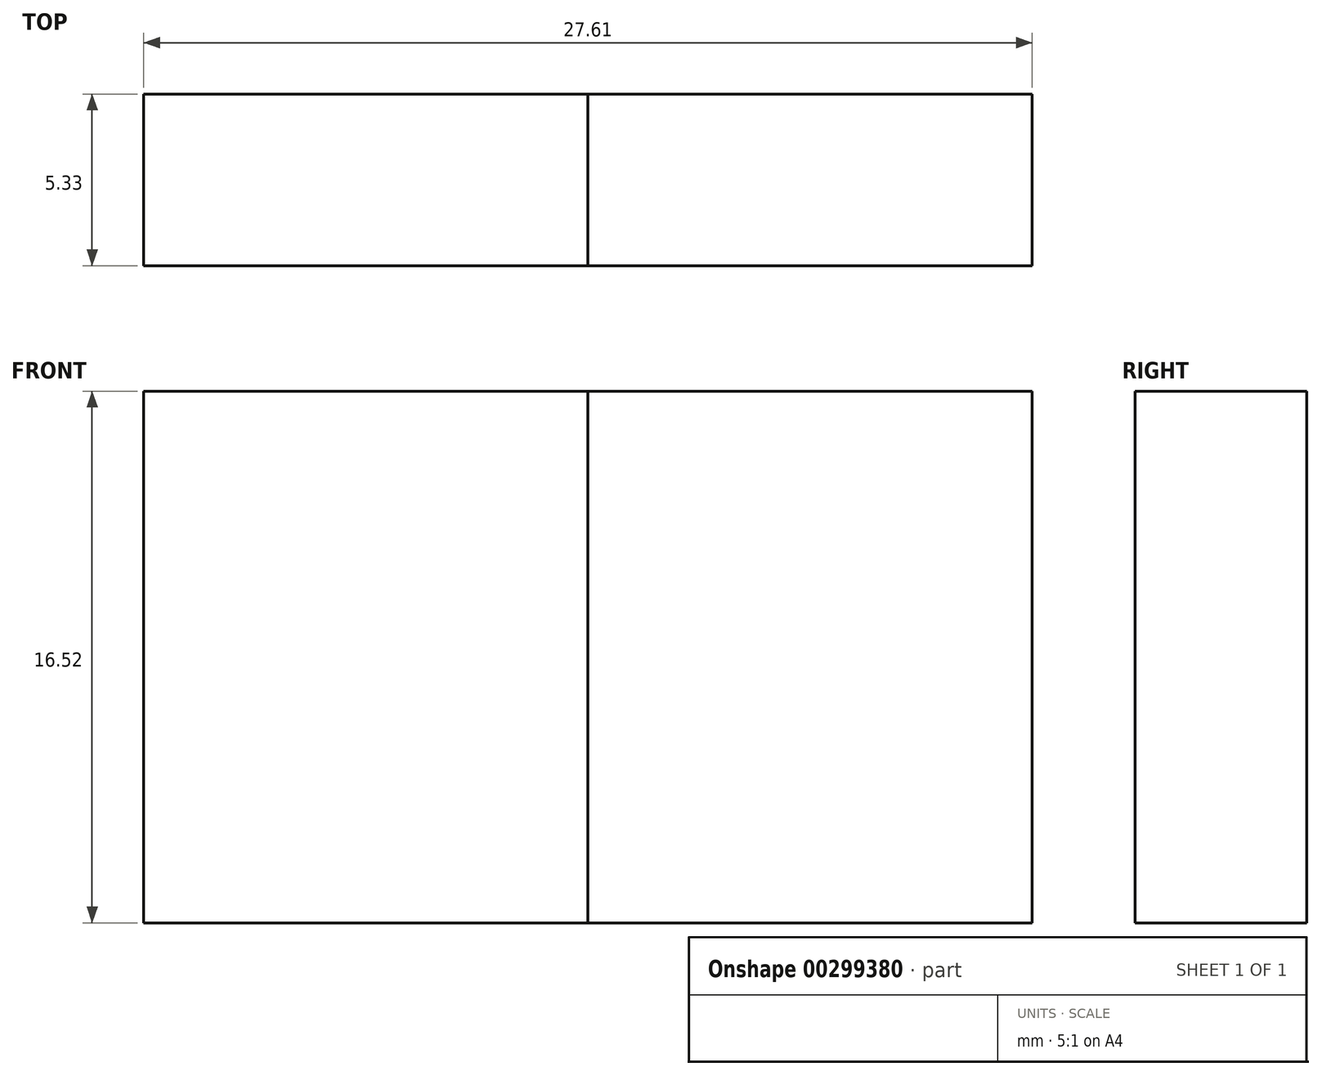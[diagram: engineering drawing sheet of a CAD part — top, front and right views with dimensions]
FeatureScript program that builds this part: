
annotation { "Feature Type Name" : "Feature", "Feature Type Description" : "" }
export const myFeature = defineFeature(function(context is Context, id is Id, definition is map)
    precondition{}
    {
        {
            var Q0;
            Q0=qCreatedBy(makeId("Front.planeOp"),FACE);
            var sketch = newSketch(context, id + "F0", { "sketchPlane" : qUnion([Q0])});
            skLineSegment(sketch, "E0.bottom", {"start": v(-35, 16.52) * mm, "end": v(-7.4, 16.52) * mm});
            skLineSegment(sketch, "E0.top", {"start": v(-35, 0) * mm, "end": v(-7.4, 0) * mm});
            skLineSegment(sketch, "E0.left", {"start": v(-35, 16.52) * mm, "end": v(-35, 0) * mm});
            skLineSegment(sketch, "E0.right", {"start": v(-7.4, 16.52) * mm, "end": v(-7.4, 0) * mm});
            skLineSegment(sketch, "E1", {"start": v(-21.2, 16.52) * mm, "end": v(-21.2, 0) * mm});
            skSolve(sketch);
        }
        {
            var Q0;
            {var subQ0=sQuery(id+"F0.wireOp",EDGE,"E0.right");Q0=makeQuery(id+"F0.imprint","IMPRINT",FACE,{"disambiguationData":[TD([[makeQuery(id+"F0.imprint","IMPRINT",EDGE,{"derivedFrom":subQ0}),-1.0]])]});}
            extrude(context, id + "F1", {"entities" : qUnion([Q0]), "depth" : 5.33 * mm});
        }
        {
            var Q0;
            {var subQ0=sQuery(id+"F0.wireOp",EDGE,"E0.left");Q0=makeQuery(id+"F0.imprint","IMPRINT",FACE,{"disambiguationData":[TD([[makeQuery(id+"F0.imprint","IMPRINT",EDGE,{"derivedFrom":subQ0}),1.0]])]});}
            extrude(context, id + "F2", {"entities" : qUnion([Q0]), "depth" : 5.33 * mm});
        }
    });
